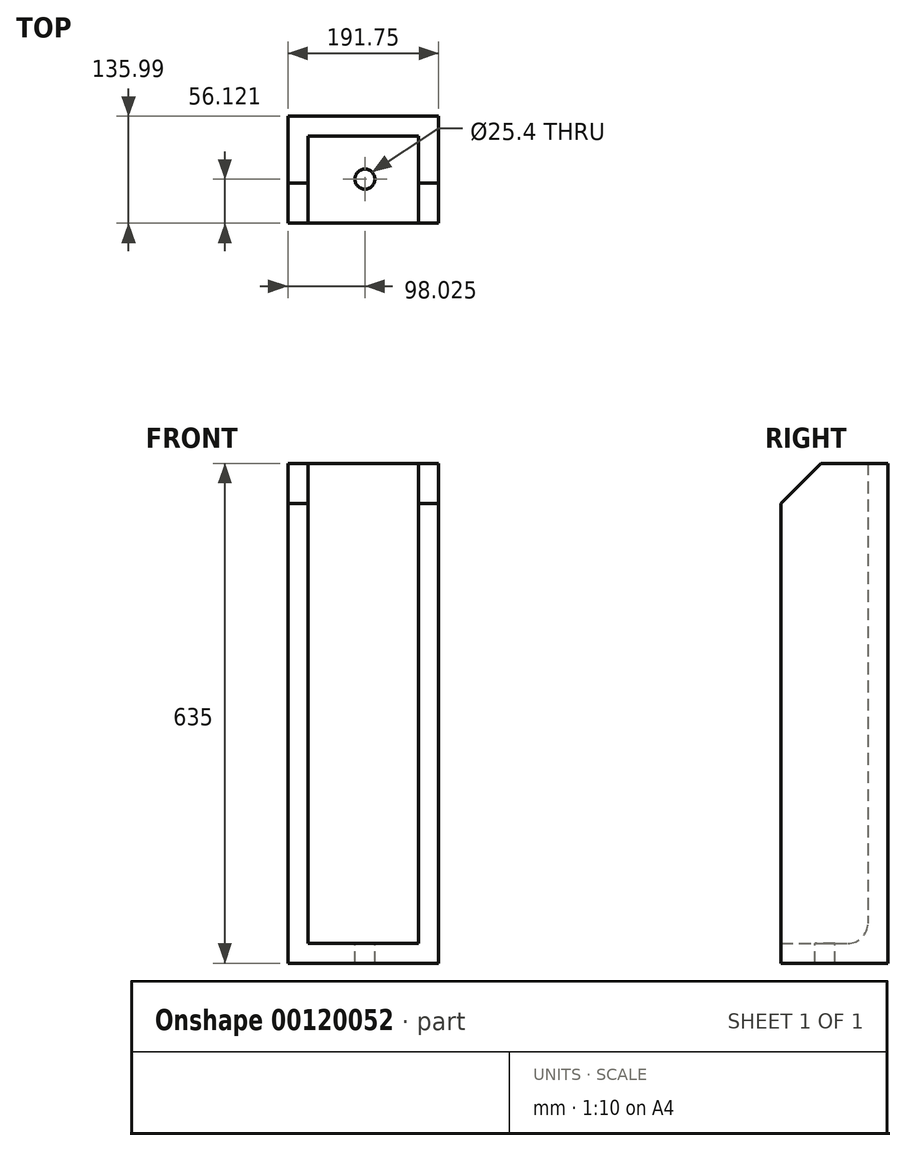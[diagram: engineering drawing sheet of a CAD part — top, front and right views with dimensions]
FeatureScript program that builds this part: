
annotation { "Feature Type Name" : "Feature", "Feature Type Description" : "" }
export const myFeature = defineFeature(function(context is Context, id is Id, definition is map)
    precondition{}
    {
        {
            var Q0;
            Q0=qCreatedBy(makeId("Top.planeOp"),FACE);
            var sketch = newSketch(context, id + "F0", { "sketchPlane" : qUnion([Q0])});
            skLineSegment(sketch, "E0.bottom", {"start": v(0, 0) * mm, "end": v(191.75, 0) * mm});
            skLineSegment(sketch, "E0.top", {"start": v(0, 136) * mm, "end": v(191.75, 136) * mm});
            skLineSegment(sketch, "E0.left", {"start": v(0, 0) * mm, "end": v(0, 136) * mm});
            skLineSegment(sketch, "E0.right", {"start": v(191.75, 0) * mm, "end": v(191.75, 136) * mm});
            skSolve(sketch);
        }
        {
            var Q0;
            Q0=makeQuery(id+"F0.imprint","IMPRINT",FACE,{"disambiguationData":[TD([[makeQuery(id+"F0.imprint","IMPRINT",EDGE,{"derivedFrom":sQuery(id+"F0.wireOp",EDGE,"E0.bottom")}),1.0]])]});
            extrude(context, id + "F1", {"entities" : qUnion([Q0]), "depth" : 635 * mm});
        }
        {
            var Q0;
            Q0=makeQuery(id+"F1.opExtrude","SWEPT_FACE",FACE,{"disambiguationData":[OSD([sQuery(id+"F0.wireOp",EDGE,"E0.bottom")])]});
            var Q1;
            Q1=makeQuery(id+"F1.opExtrude","CAP_FACE",FACE,{"disambiguationData":[OSD([sQuery(id+"F0.wireOp",EDGE,"E0.bottom"),sQuery(id+"F0.wireOp",EDGE,"E0.top"),sQuery(id+"F0.wireOp",EDGE,"E0.left"),sQuery(id+"F0.wireOp",EDGE,"E0.right")])],"isStart":false});
            shell(context, id + "F2", {"entities" : qUnion([Q0, Q1]), "thickness" : 25.4 * mm});
        }
        {
            var Q0;
            Q0=makeQuery(id+"F2.opShell","OFFSET_FACE",FACE,{"disambiguationData":[OSD([sQuery(id+"F0.wireOp",EDGE,"E0.bottom"),sQuery(id+"F0.wireOp",EDGE,"E0.top"),sQuery(id+"F0.wireOp",EDGE,"E0.left"),sQuery(id+"F0.wireOp",EDGE,"E0.right")])]});
            var sketch = newSketch(context, id + "F3", { "sketchPlane" : qUnion([Q0])});
            skPoint(sketch, "E1", {"position": v(98.02, 56.12) * mm});
            skSolve(sketch);
        }
        {
            var Q0;
            Q0=sQuery(id+"F3.wireOp",VERTEX,"E1");
            var Q1;
            Q1=makeQuery(id+"F1.opExtrude","SWEPT_BODY",BODY,{"disambiguationData":[OSD([sQuery(id+"F0.wireOp",EDGE,"E0.bottom"),sQuery(id+"F0.wireOp",EDGE,"E0.top"),sQuery(id+"F0.wireOp",EDGE,"E0.left"),sQuery(id+"F0.wireOp",EDGE,"E0.right")])]});
            hole(context, id + "F4", {"style" : HoleStyle.SIMPLE, "endStyle" : HoleEndStyle.THROUGH, "holeDiameter" : 25.4 * mm, "locations" : qUnion([Q0]), "scope" : qUnion([Q1]), "isTappedThrough" : true});
        }
        {
            var Q0;
            {var subQ0=sQuery(id+"F0.wireOp",EDGE,"E0.top");Q0=makeQuery(id+"F2.opShell","OFFSET_EDGE",EDGE,{"disambiguationData":[OSD([subQ0]),TDD([makeQuery(id+"F1.opExtrude","CAP_EDGE",EDGE,{"disambiguationData":[OSD([subQ0])],"isStart":true})])]});}
            fillet(context, id + "F5", {"entities" : qUnion([Q0]), "radius" : 25.4 * mm, "tangentPropagation" : true, "allowEdgeOverflow" : false});
        }
        {
            var Q0;
            {var subQ0=sQuery(id+"F0.wireOp",EDGE,"E0.bottom");Q0=makeQuery(id+"F2.opShell","OFFSET_EDGE",EDGE,{"disambiguationData":[OSD([subQ0]),TDD([makeQuery(id+"F1.opExtrude","CAP_EDGE",EDGE,{"disambiguationData":[OSD([subQ0])],"isStart":false})])]});}
            var Q1;
            Q1=makeQuery(id+"F1.opExtrude","CAP_EDGE",EDGE,{"disambiguationData":[OSD([sQuery(id+"F0.wireOp",EDGE,"E0.bottom")])],"isStart":false});
            chamfer(context, id + "F6", {"entities" : qUnion([Q0, Q1]), "width" : 50.8 * mm, "tangentPropagation" : true});
        }
    });
